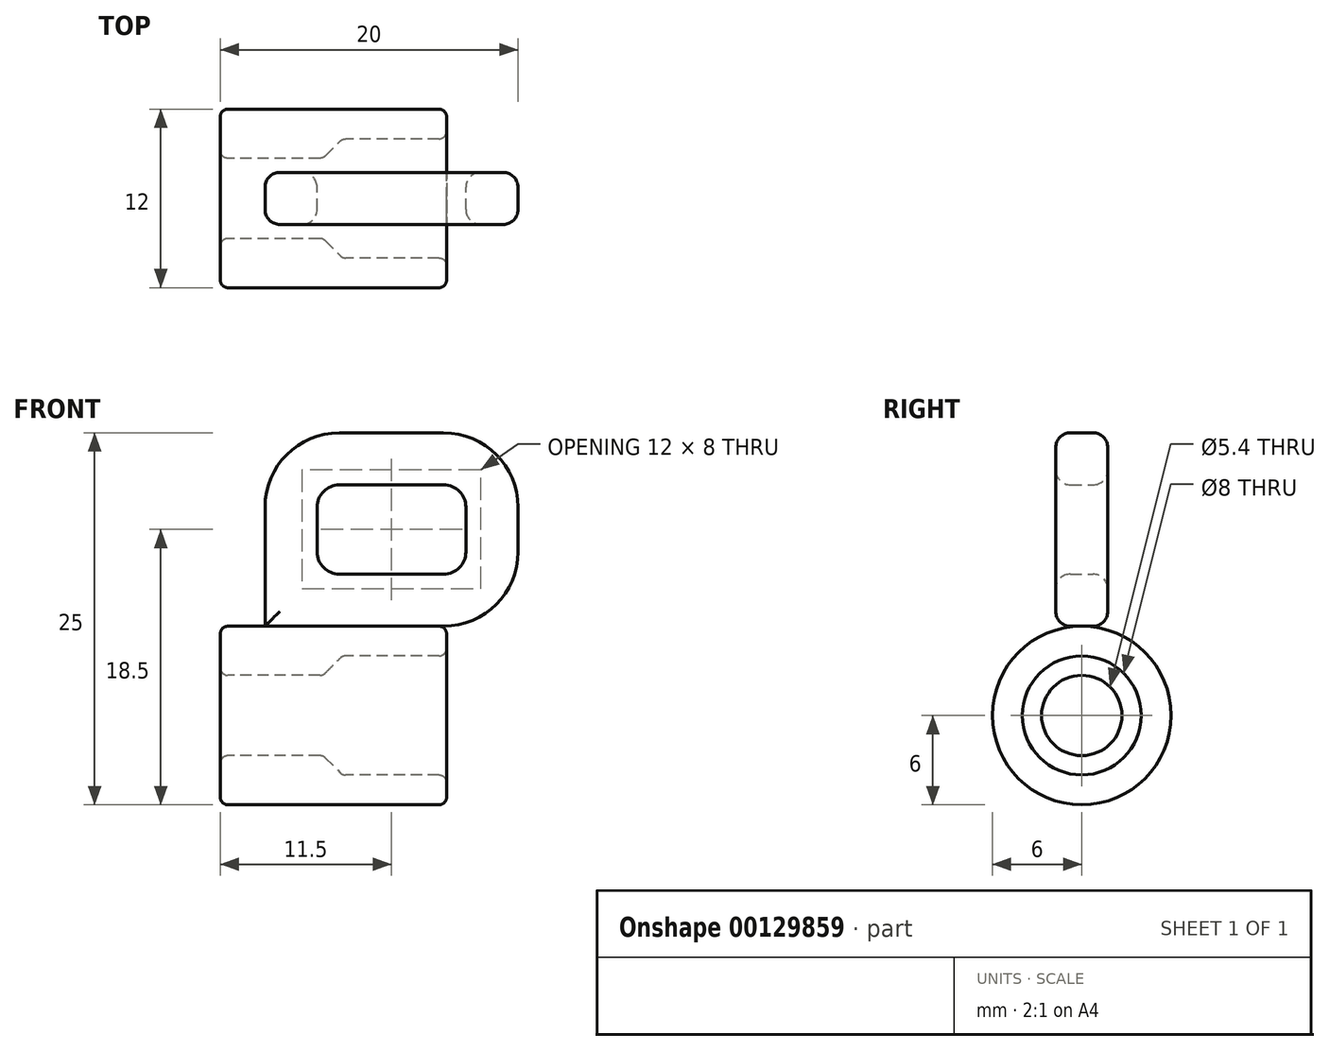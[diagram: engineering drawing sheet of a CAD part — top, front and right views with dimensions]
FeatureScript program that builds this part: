
annotation { "Feature Type Name" : "Feature", "Feature Type Description" : "" }
export const myFeature = defineFeature(function(context is Context, id is Id, definition is map)
    precondition{}
    {
        {
            var Q0;
            Q0=qCreatedBy(makeId("Front.planeOp"),FACE);
            var sketch = newSketch(context, id + "F0", { "sketchPlane" : qUnion([Q0])});
            skLineSegment(sketch, "E0", {"start": v(-46.25, 0) * mm, "end": v(41.44, 0) * mm, "construction": true});
            skLineSegment(sketch, "E1", {"start": v(-7.1, 6) * mm, "end": v(7.1, 6) * mm});
            skPoint(sketch, "E2", {"position": v(0, 6) * mm});
            skLineSegment(sketch, "E3", {"start": v(0, 6) * mm, "end": v(0, 0) * mm, "construction": true});
            skLineSegment(sketch, "E4", {"start": v(-7.6, 5.5) * mm, "end": v(-7.6, 3.2) * mm});
            skLineSegment(sketch, "E5", {"start": v(7.6, 5.5) * mm, "end": v(7.6, 4.5) * mm});
            skLineSegment(sketch, "E6", {"start": v(7.1, 4) * mm, "end": v(0.8, 4) * mm});
            skLineSegment(sketch, "E7", {"start": v(-7.1, 2.7) * mm, "end": v(-0.9, 2.7) * mm});
            skLineSegment(sketch, "E8", {"start": v(-0.55, 2.85) * mm, "end": v(0.45, 3.85) * mm});
            skLineSegment(sketch, "E9", {"start": v(-0.7, 2.7) * mm, "end": v(-0.7, 4.88) * mm, "construction": true});
            skPoint(sketch, "E10.visualSharp", {"position": v(7.6, 6) * mm});
            skArc(sketch, "E10.filletArc", {"start": v(7.6, 5.5) * mm, "mid": v(7.45, 5.85) * mm, "end": v(7.1, 6) * mm});
            skPoint(sketch, "E11.visualSharp", {"position": v(7.6, 4) * mm});
            skArc(sketch, "E11.filletArc", {"start": v(7.1, 4) * mm, "mid": v(7.45, 4.15) * mm, "end": v(7.6, 4.5) * mm});
            skPoint(sketch, "E12.visualSharp", {"position": v(-7.6, 6) * mm});
            skArc(sketch, "E12.filletArc", {"start": v(-7.1, 6) * mm, "mid": v(-7.45, 5.85) * mm, "end": v(-7.6, 5.5) * mm});
            skPoint(sketch, "E13.visualSharp", {"position": v(-7.6, 2.7) * mm});
            skArc(sketch, "E13.filletArc", {"start": v(-7.6, 3.2) * mm, "mid": v(-7.45, 2.85) * mm, "end": v(-7.1, 2.7) * mm});
            skPoint(sketch, "E14.visualSharp", {"position": v(-0.7, 2.7) * mm});
            skArc(sketch, "E14.filletArc", {"start": v(-0.9, 2.7) * mm, "mid": v(-0.72, 2.74) * mm, "end": v(-0.55, 2.85) * mm});
            skPoint(sketch, "E15.visualSharp", {"position": v(0.6, 4) * mm});
            skArc(sketch, "E15.filletArc", {"start": v(0.8, 4) * mm, "mid": v(0.62, 3.96) * mm, "end": v(0.45, 3.85) * mm});
            skSolve(sketch);
        }
        {
            var Q0;
            Q0=qCreatedBy(makeId("Front.planeOp"),FACE);
            var sketch = newSketch(context, id + "F1", { "sketchPlane" : qUnion([Q0])});
            skLineSegment(sketch, "E16", {"start": v(-4.6, 6) * mm, "end": v(-4.6, 8.28) * mm});
            skLineSegment(sketch, "E17", {"start": v(-4.6, 6) * mm, "end": v(7.4, 6) * mm});
            skLineSegment(sketch, "E18", {"start": v(12.4, 11) * mm, "end": v(12.4, 14) * mm});
            skLineSegment(sketch, "E19", {"start": v(7.4, 19) * mm, "end": v(0.4, 19) * mm});
            skLineSegment(sketch, "E20", {"start": v(-4.6, 14) * mm, "end": v(-4.6, 8.28) * mm});
            skPoint(sketch, "E21.visualSharp", {"position": v(-4.6, 19) * mm});
            skArc(sketch, "E21.filletArc", {"start": v(0.4, 19) * mm, "mid": v(-3.14, 17.54) * mm, "end": v(-4.6, 14) * mm});
            skPoint(sketch, "E22.visualSharp", {"position": v(12.4, 19) * mm});
            skArc(sketch, "E22.filletArc", {"start": v(12.4, 14) * mm, "mid": v(10.94, 17.54) * mm, "end": v(7.4, 19) * mm});
            skPoint(sketch, "E23.visualSharp", {"position": v(12.4, 6) * mm});
            skArc(sketch, "E23.filletArc", {"start": v(7.4, 6) * mm, "mid": v(10.94, 7.46) * mm, "end": v(12.4, 11) * mm});
            skArc(sketch, "E24.0", {"start": v(8.9, 14) * mm, "mid": v(8.46, 15.06) * mm, "end": v(7.4, 15.5) * mm});
            skLineSegment(sketch, "E24.1", {"start": v(8.9, 11) * mm, "end": v(8.9, 14) * mm});
            skArc(sketch, "E24.2", {"start": v(0.4, 15.5) * mm, "mid": v(-0.66, 15.06) * mm, "end": v(-1.1, 14) * mm});
            skLineSegment(sketch, "E24.3", {"start": v(-1.1, 14) * mm, "end": v(-1.1, 11) * mm});
            skLineSegment(sketch, "E24.4", {"start": v(0.4, 9.5) * mm, "end": v(7.4, 9.5) * mm});
            skLineSegment(sketch, "E24.5", {"start": v(7.4, 15.5) * mm, "end": v(0.4, 15.5) * mm});
            skArc(sketch, "E24.6", {"start": v(7.4, 9.5) * mm, "mid": v(8.46, 9.94) * mm, "end": v(8.9, 11) * mm});
            skPoint(sketch, "E25.visualSharp", {"position": v(-1.1, 9.5) * mm});
            skArc(sketch, "E25.filletArc", {"start": v(-1.1, 11) * mm, "mid": v(-0.66, 9.94) * mm, "end": v(0.4, 9.5) * mm});
            skSolve(sketch);
        }
        {
            var Q0;
            Q0=makeQuery(id+"F1.imprint","IMPRINT",FACE,{"disambiguationData":[TD([[makeQuery(id+"F1.imprint","IMPRINT",EDGE,{"derivedFrom":sQuery(id+"F1.wireOp",EDGE,"E16")}),-1.0]])]});
            extrude(context, id + "F2", {"entities" : qUnion([Q0]), "endBound" : BoundingType.SYMMETRIC, "depth" : 3.5 * mm});
        }
        {
            var Q0;
            Q0=makeQuery(id+"F0.imprint","IMPRINT",FACE,{"disambiguationData":[TD([[makeQuery(id+"F0.imprint","IMPRINT",EDGE,{"derivedFrom":sQuery(id+"F0.wireOp",EDGE,"E1")}),-1.0]])]});
            var Q1;
            Q1=sQuery(id+"F0.wireOp",EDGE,"E0");
            revolve(context, id + "F3", {"entities" : qUnion([Q0]), "axis" : qUnion([Q1]), "revolveType" : RevolveType.FULL});
        }
        {
            var Q0;
            Q0=makeQuery(id+"F2.opExtrude","CAP_EDGE",EDGE,{"disambiguationData":[OSD([sQuery(id+"F1.wireOp",EDGE,"E19")])],"isStart":false});
            var Q1;
            Q1=makeQuery(id+"F2.opExtrude","CAP_EDGE",EDGE,{"disambiguationData":[OSD([sQuery(id+"F1.wireOp",EDGE,"E24.5")])],"isStart":false});
            var Q2;
            Q2=makeQuery(id+"F2.opExtrude","CAP_EDGE",EDGE,{"disambiguationData":[OSD([sQuery(id+"F1.wireOp",EDGE,"E24.3")])],"isStart":true});
            var Q3;
            Q3=makeQuery(id+"F2.opExtrude","CAP_EDGE",EDGE,{"disambiguationData":[OSD([sQuery(id+"F1.wireOp",EDGE,"E22.filletArc")])],"isStart":true});
            fillet(context, id + "F4", {"entities" : qUnion([Q0, Q1, Q2, Q3]), "radius" : 1 * mm, "tangentPropagation" : true, "allowEdgeOverflow" : false});
        }
    });
